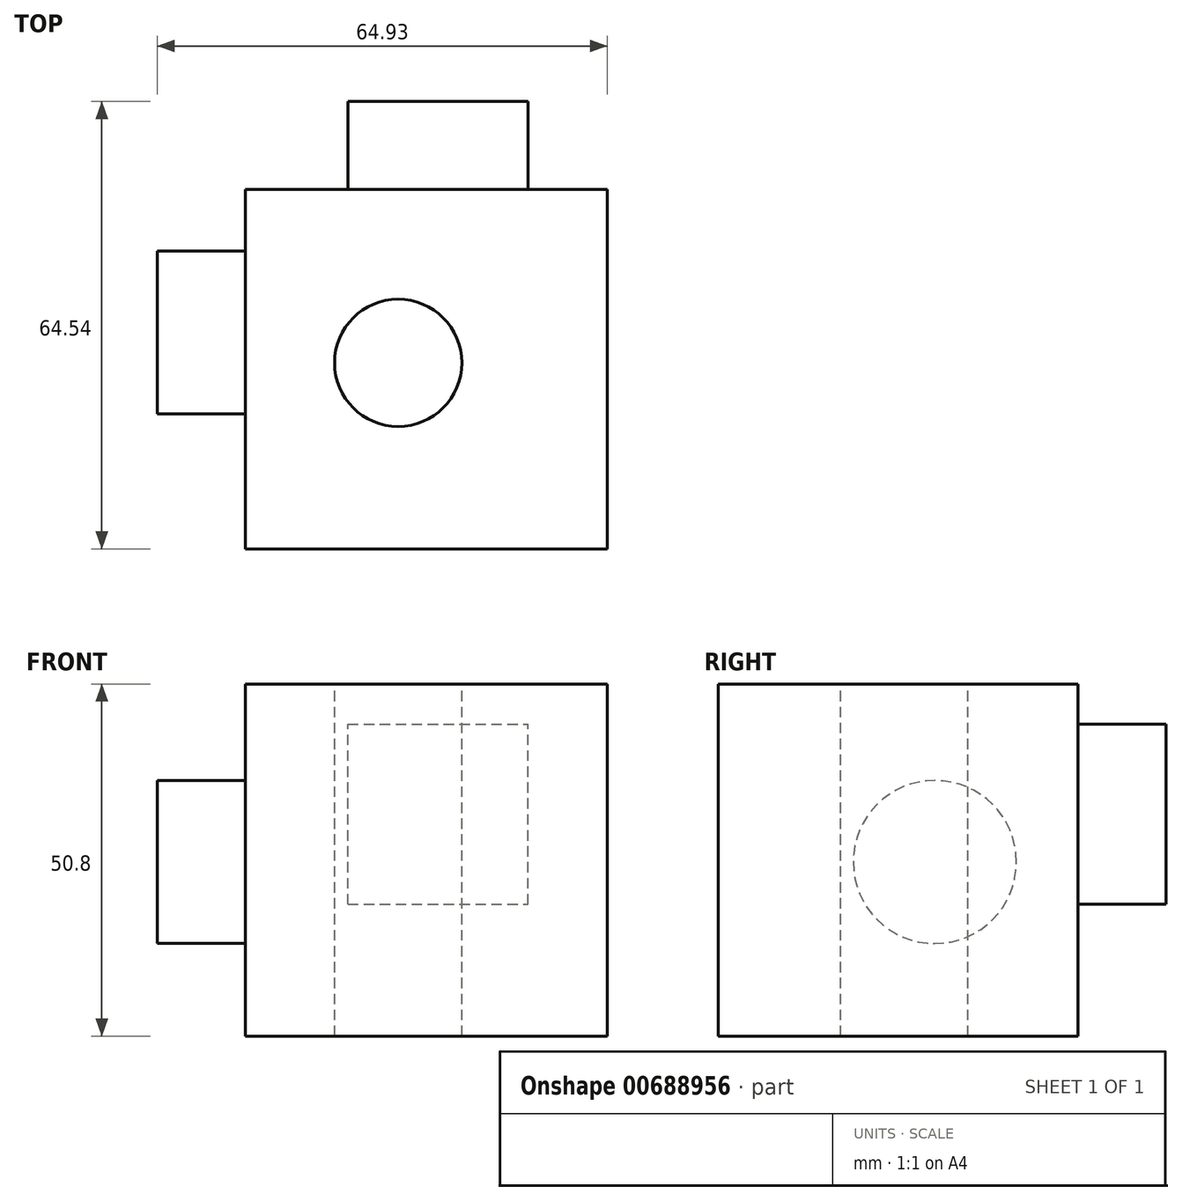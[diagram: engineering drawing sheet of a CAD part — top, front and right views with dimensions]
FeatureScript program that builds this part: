
annotation { "Feature Type Name" : "Feature", "Feature Type Description" : "" }
export const myFeature = defineFeature(function(context is Context, id is Id, definition is map)
    precondition{}
    {
        {
            var Q0;
            Q0=qCreatedBy(makeId("Top.planeOp"),FACE);
            var sketch = newSketch(context, id + "F0", { "sketchPlane" : qUnion([Q0])});
            skLineSegment(sketch, "E0.bottom", {"start": v(0, 0) * mm, "end": v(52.23, 0) * mm});
            skLineSegment(sketch, "E0.top", {"start": v(0, 51.84) * mm, "end": v(52.23, 51.84) * mm});
            skLineSegment(sketch, "E0.left", {"start": v(0, 0) * mm, "end": v(0, 51.84) * mm});
            skLineSegment(sketch, "E0.right", {"start": v(52.23, 0) * mm, "end": v(52.23, 51.84) * mm});
            skSolve(sketch);
        }
        {
            var Q0;
            Q0 = qSketchRegion(id + "F0", true);
            extrude(context, id + "F1", {"entities" : qUnion([Q0]), "depth" : 50.8 * mm, "offsetDistance" : 25.4 * mm});
        }
        {
            var Q0;
            Q0=makeQuery(id+"F1.opExtrude","CAP_FACE",FACE,{"disambiguationData":[OSD([sQuery(id+"F0.wireOp",EDGE,"E0.bottom"),sQuery(id+"F0.wireOp",EDGE,"E0.top"),sQuery(id+"F0.wireOp",EDGE,"E0.left"),sQuery(id+"F0.wireOp",EDGE,"E0.right")])],"isStart":false});
            var sketch = newSketch(context, id + "F2", { "sketchPlane" : qUnion([Q0])});
            skCircle(sketch, "E1", {"center": v(22.06, 26.83) * mm, "radius": 9.18 * mm});
            skSolve(sketch);
        }
        {
            var Q0;
            Q0 = qSketchRegion(id + "F2", true);
            extrude(context, id + "F3", {"entities" : qUnion([Q0]), "operationType" : NewBodyOperationType.REMOVE, "oppositeDirection" : true, "depth" : 58.67 * mm, "offsetDistance" : 25.4 * mm});
        }
        {
            var Q0;
            Q0=makeQuery(id+"F1.opExtrude","SWEPT_FACE",FACE,{"disambiguationData":[OSD([sQuery(id+"F0.wireOp",EDGE,"E0.top")])]});
            var sketch = newSketch(context, id + "F4", { "sketchPlane" : qUnion([Q0])});
            skLineSegment(sketch, "E2.bottom", {"start": v(-14.8, 19) * mm, "end": v(-40.77, 19) * mm});
            skLineSegment(sketch, "E2.top", {"start": v(-14.8, 44.97) * mm, "end": v(-40.77, 44.97) * mm});
            skLineSegment(sketch, "E2.left", {"start": v(-14.8, 19) * mm, "end": v(-14.8, 44.97) * mm});
            skLineSegment(sketch, "E2.right", {"start": v(-40.77, 19) * mm, "end": v(-40.77, 44.97) * mm});
            skSolve(sketch);
        }
        {
            var Q0;
            Q0 = qSketchRegion(id + "F4", true);
            extrude(context, id + "F5", {"entities" : qUnion([Q0]), "operationType" : NewBodyOperationType.ADD, "depth" : 12.7 * mm, "offsetDistance" : 25.4 * mm});
        }
        {
            var Q0;
            Q0=makeQuery(id+"F1.opExtrude","SWEPT_FACE",FACE,{"disambiguationData":[OSD([sQuery(id+"F0.wireOp",EDGE,"E0.left")])]});
            var sketch = newSketch(context, id + "F6", { "sketchPlane" : qUnion([Q0])});
            skCircle(sketch, "E3", {"center": v(-31.22, 25.11) * mm, "radius": 11.77 * mm});
            skSolve(sketch);
        }
        {
            var Q0;
            Q0 = qSketchRegion(id + "F6", true);
            extrude(context, id + "F7", {"entities" : qUnion([Q0]), "operationType" : NewBodyOperationType.ADD, "depth" : 12.7 * mm, "offsetDistance" : 25.4 * mm});
        }
    });
